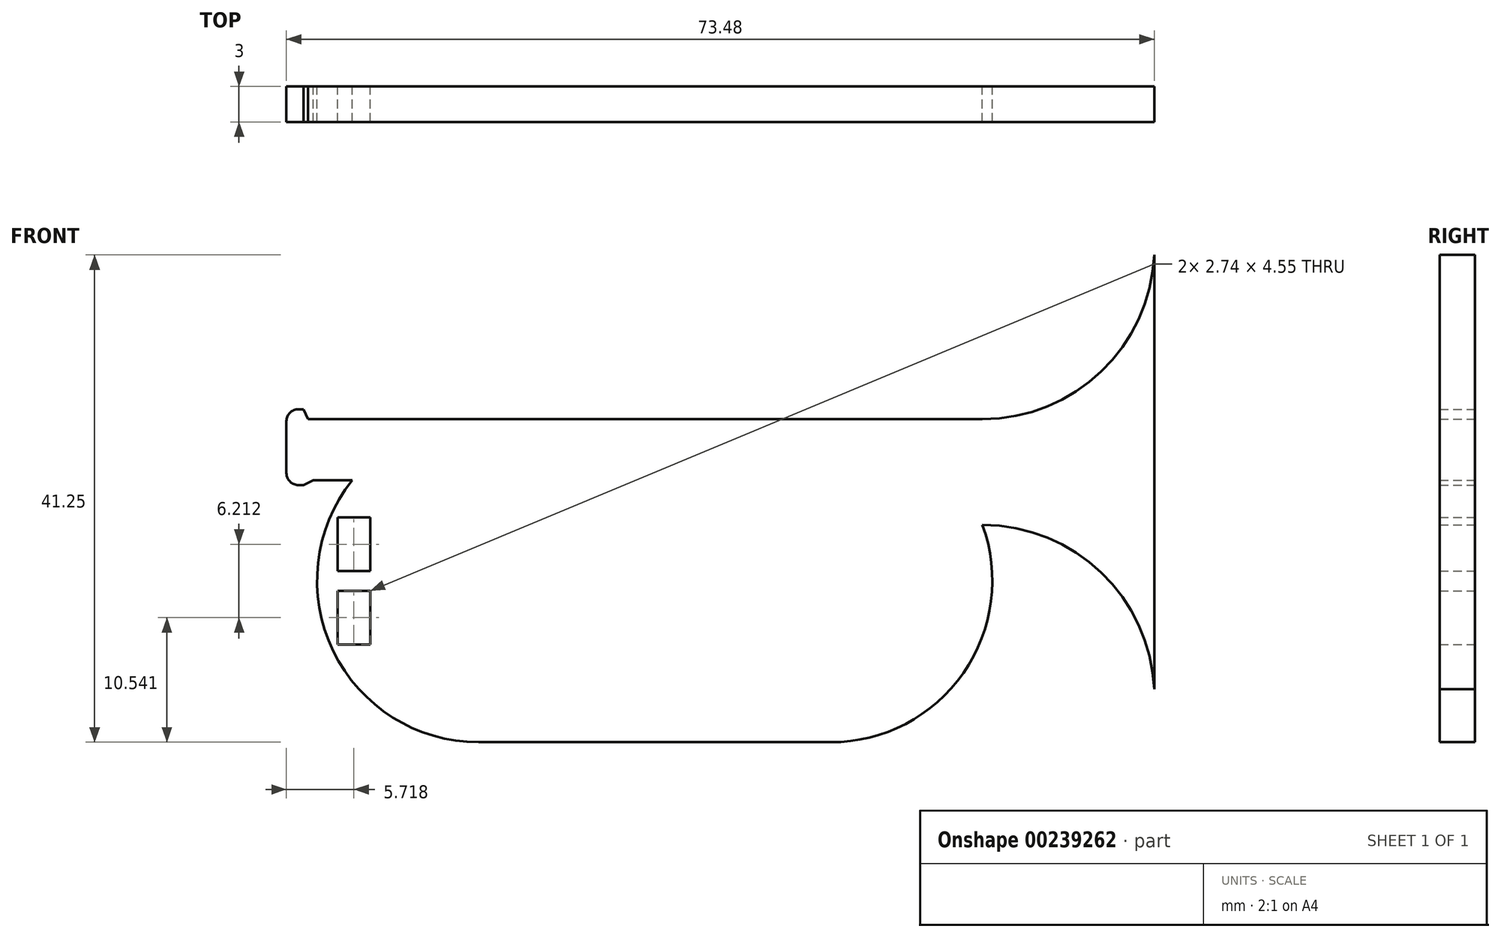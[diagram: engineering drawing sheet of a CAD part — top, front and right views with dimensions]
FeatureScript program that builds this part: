
annotation { "Feature Type Name" : "Feature", "Feature Type Description" : "" }
export const myFeature = defineFeature(function(context is Context, id is Id, definition is map)
    precondition{}
    {
        {
            var Q0;
            Q0=qCreatedBy(makeId("Front.planeOp"),FACE);
            var sketch = newSketch(context, id + "F0", { "sketchPlane" : qUnion([Q0])});
            skArc(sketch, "E0", {"start": v(-10.7, 8.5) * mm, "mid": v(-12.3, -5.95) * mm, "end": v(0, -13.67) * mm});
            skArc(sketch, "E1", {"start": v(29.83, -13.67) * mm, "mid": v(41.04, -7.82) * mm, "end": v(42.66, 4.72) * mm});
            skLineSegment(sketch, "E2", {"start": v(0, 13.67) * mm, "end": v(29.83, 13.67) * mm});
            skLineSegment(sketch, "E3", {"start": v(0, -13.67) * mm, "end": v(29.83, -13.67) * mm});
            skLineSegment(sketch, "E4", {"start": v(0, 13.67) * mm, "end": v(-14.43, 13.67) * mm});
            skLineSegment(sketch, "E5", {"start": v(-14.43, 13.67) * mm, "end": v(-14.83, 14.51) * mm});
            skLineSegment(sketch, "E6", {"start": v(-14.83, 14.51) * mm, "end": v(-15.27, 14.51) * mm});
            skLineSegment(sketch, "E7", {"start": v(-16.27, 13.51) * mm, "end": v(-16.27, 9.1) * mm});
            skLineSegment(sketch, "E8", {"start": v(-15.27, 8.1) * mm, "end": v(-14.83, 8.1) * mm});
            skLineSegment(sketch, "E9", {"start": v(-14.83, 8.1) * mm, "end": v(-13.99, 8.5) * mm});
            skLineSegment(sketch, "E10", {"start": v(-13.99, 8.5) * mm, "end": v(-10.7, 8.5) * mm});
            skPoint(sketch, "E11.visualSharp", {"position": v(-16.27, 14.51) * mm});
            skArc(sketch, "E11.filletArc", {"start": v(-15.27, 14.51) * mm, "mid": v(-15.98, 14.22) * mm, "end": v(-16.27, 13.51) * mm});
            skPoint(sketch, "E12.visualSharp", {"position": v(-16.27, 8.1) * mm});
            skArc(sketch, "E12.filletArc", {"start": v(-16.27, 9.1) * mm, "mid": v(-15.98, 8.4) * mm, "end": v(-15.27, 8.1) * mm});
            skLineSegment(sketch, "E13", {"start": v(29.83, 13.67) * mm, "end": v(42.66, 13.67) * mm});
            skLineSegment(sketch, "E14", {"start": v(42.66, 4.72) * mm, "end": v(42.66, 4.72) * mm});
            skLineSegment(sketch, "E15", {"start": v(42.66, 13.67) * mm, "end": v(42.66, 4.72) * mm, "construction": true});
            skArc(sketch, "E16", {"start": v(42.66, 13.67) * mm, "mid": v(53.19, 18.17) * mm, "end": v(57.21, 28.88) * mm});
            skArc(sketch, "E17", {"start": v(57.21, -9.2) * mm, "mid": v(52.73, 0.68) * mm, "end": v(42.66, 4.72) * mm});
            skLineSegment(sketch, "E18", {"start": v(42.66, 28.23) * mm, "end": v(42.66, -9.84) * mm, "construction": true});
            skLineSegment(sketch, "E19", {"start": v(57.21, 28.88) * mm, "end": v(57.21, -9.2) * mm});
            skLineSegment(sketch, "E20.bottom", {"start": v(-11.92, 5.36) * mm, "end": v(-9.18, 5.36) * mm});
            skLineSegment(sketch, "E20.top", {"start": v(-11.92, -5.4) * mm, "end": v(-9.18, -5.4) * mm});
            skLineSegment(sketch, "E20.left", {"start": v(-11.92, 5.36) * mm, "end": v(-11.92, 0.8) * mm});
            skLineSegment(sketch, "E20.right", {"start": v(-9.18, 5.36) * mm, "end": v(-9.18, 0.8) * mm});
            skPoint(sketch, "E21.endSnap0", {"position": v(-9.18, -0.02) * mm});
            skLineSegment(sketch, "E22.trimOffspring", {"start": v(-11.92, -0.86) * mm, "end": v(-11.92, -5.4) * mm});
            skLineSegment(sketch, "E23.trimOffspring", {"start": v(-9.18, -0.86) * mm, "end": v(-9.18, -5.4) * mm});
            skLineSegment(sketch, "E24", {"start": v(-11.92, 0.8) * mm, "end": v(-9.18, 0.8) * mm});
            skLineSegment(sketch, "E25", {"start": v(-11.92, -0.86) * mm, "end": v(-9.18, -0.86) * mm});
            skPoint(sketch, "E26.orphan", {"position": v(-9.18, 0) * mm});
            skPoint(sketch, "E27.orphan", {"position": v(-11.92, -0.02) * mm});
            skSolve(sketch);
        }
        {
            var Q0;
            Q0=makeQuery(id+"F0.imprint","IMPRINT",FACE,{"disambiguationData":[TD([[makeQuery(id+"F0.imprint","IMPRINT",EDGE,{"derivedFrom":sQuery(id+"F0.wireOp",EDGE,"E0")}),1.0]])]});
            extrude(context, id + "F1", {"entities" : qUnion([Q0]), "depth" : 3 * mm});
        }
    });
